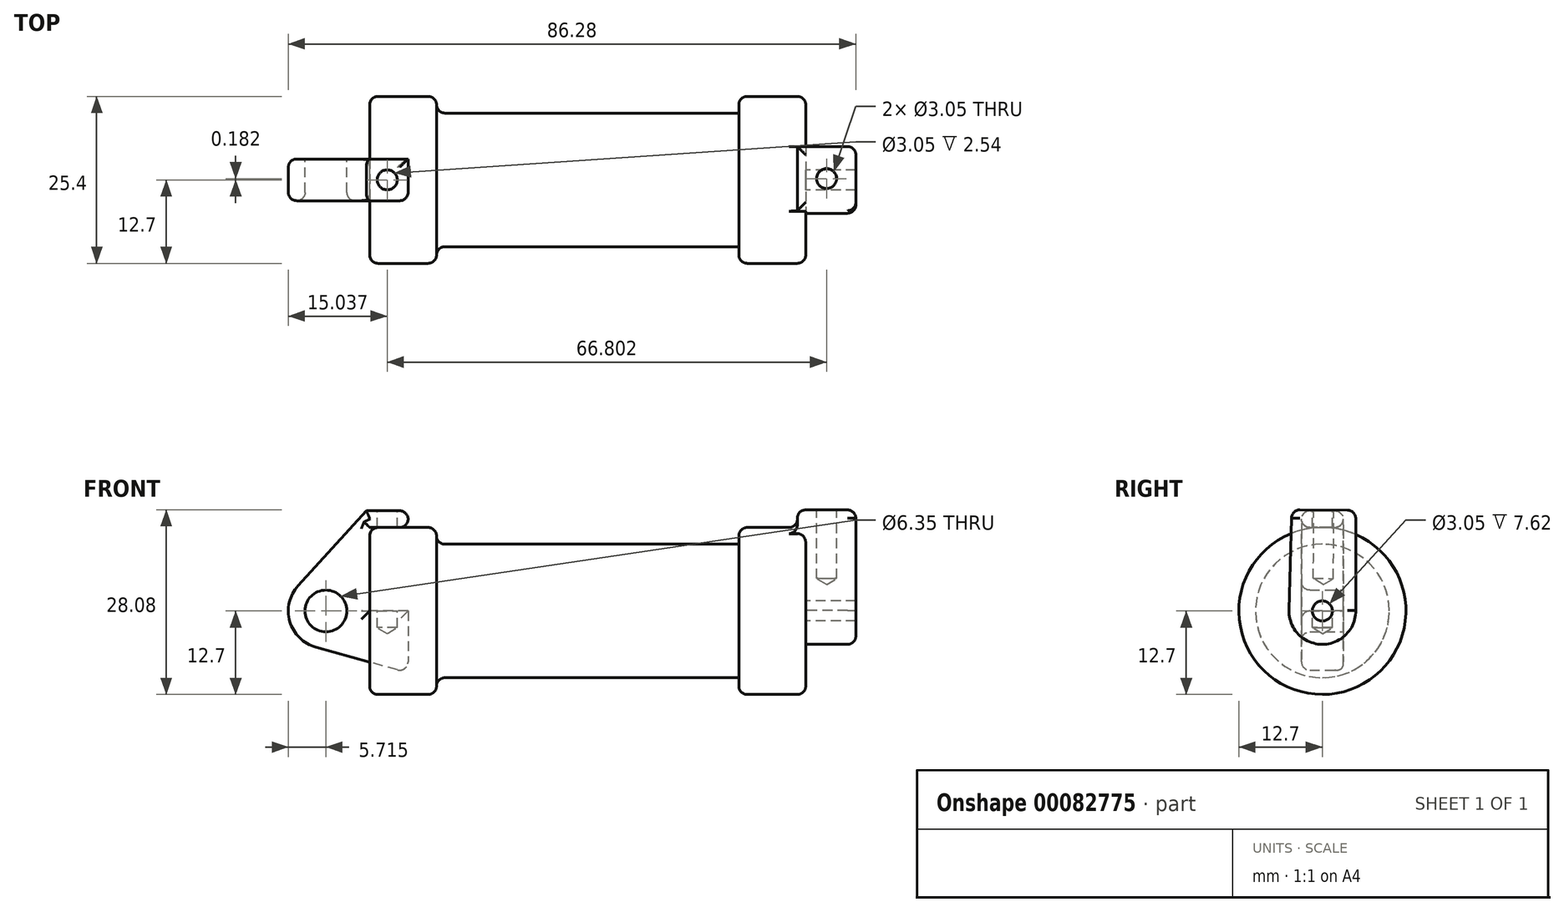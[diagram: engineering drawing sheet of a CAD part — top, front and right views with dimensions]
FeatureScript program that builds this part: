
annotation { "Feature Type Name" : "Feature", "Feature Type Description" : "" }
export const myFeature = defineFeature(function(context is Context, id is Id, definition is map)
    precondition{}
    {
        {
            var Q0;
            Q0=qCreatedBy(makeId("Front.planeOp"),FACE);
            var sketch = newSketch(context, id + "F0", { "sketchPlane" : qUnion([Q0])});
            skLineSegment(sketch, "E0", {"start": v(0, 0) * mm, "end": v(0, 12.7) * mm});
            skLineSegment(sketch, "E1", {"start": v(0, 12.7) * mm, "end": v(10.16, 12.7) * mm});
            skLineSegment(sketch, "E2", {"start": v(10.16, 12.7) * mm, "end": v(10.16, 10.16) * mm});
            skLineSegment(sketch, "E3", {"start": v(10.16, 10.16) * mm, "end": v(56.13, 10.16) * mm});
            skLineSegment(sketch, "E4", {"start": v(56.13, 10.16) * mm, "end": v(56.13, 12.7) * mm});
            skLineSegment(sketch, "E5", {"start": v(56.13, 12.7) * mm, "end": v(66.3, 12.7) * mm});
            skLineSegment(sketch, "E6", {"start": v(66.3, 12.7) * mm, "end": v(66.3, 0) * mm});
            skLineSegment(sketch, "E7", {"start": v(66.3, 0) * mm, "end": v(0, 0) * mm});
            skLineSegment(sketch, "E8", {"start": v(5.84, 15.24) * mm, "end": v(-0.5, 15.24) * mm});
            skLineSegment(sketch, "E9", {"start": v(-0.5, 15.24) * mm, "end": v(-10.88, 3.85) * mm});
            skLineSegment(sketch, "E10", {"start": v(0, 0) * mm, "end": v(-6.65, 0) * mm});
            skCircle(sketch, "E11", {"center": v(-6.65, 0) * mm, "radius": 5.72 * mm});
            skCircle(sketch, "E12", {"center": v(-6.65, 0) * mm, "radius": 3.18 * mm});
            skLineSegment(sketch, "E13", {"start": v(5.84, 15.24) * mm, "end": v(5.84, -9.4) * mm});
            skLineSegment(sketch, "E14", {"start": v(5.84, -9.4) * mm, "end": v(-8.18, -5.5) * mm});
            skSolve(sketch);
        }
        {
            var Q0;
            {var subQ0=sQuery(id+"F0.wireOp",EDGE,"E2");Q0=makeQuery(id+"F0.imprint","IMPRINT",FACE,{"disambiguationData":[TD([[makeQuery(id+"F0.imprint","IMPRINT",EDGE,{"derivedFrom":subQ0}),-1.0]])]});}
            var Q1;
            {var subQ0=sQuery(id+"F0.wireOp",EDGE,"E0");Q1=makeQuery(id+"F0.imprint","IMPRINT",FACE,{"disambiguationData":[TD([[makeQuery(id+"F0.imprint","IMPRINT",EDGE,{"derivedFrom":subQ0}),-1.0]])]});}
            var Q2;
            Q2=sQuery(id+"F0.wireOp",EDGE,"E7");
            revolve(context, id + "F1", {"entities" : qUnion([Q0, Q1]), "axis" : qUnion([Q2]), "revolveType" : RevolveType.FULL});
        }
        {
            var Q0;
            {var subQ3=sQuery(id+"F0.wireOp",EDGE,"E0");Q0=makeQuery(id+"F0.imprint","IMPRINT",FACE,{"disambiguationData":[TD([[makeQuery(id+"F0.imprint","IMPRINT",EDGE,{"derivedFrom":subQ3}),1.0]])]});}
            var Q1;
            {var subQ4=sQuery(id+"F0.wireOp",EDGE,"E12");Q1=makeQuery(id+"F0.imprint","IMPRINT",FACE,{"disambiguationData":[TD([[makeQuery(id+"F0.imprint","IMPRINT",EDGE,{"derivedFrom":subQ4}),-1.0]])]});}
            var Q2;
            {var subQ0=sQuery(id+"F0.wireOp",EDGE,"E14");Q2=makeQuery(id+"F0.imprint","IMPRINT",FACE,{"disambiguationData":[TD([[makeQuery(id+"F0.imprint","IMPRINT",EDGE,{"derivedFrom":subQ0}),-1.0]])]});}
            extrude(context, id + "F2", {"entities" : qUnion([Q0, Q1, Q2]), "endBound" : BoundingType.SYMMETRIC, "depth" : 6.35 * mm});
        }
        {
            var Q0;
            Q0=makeQuery(id+"F1.opRevolve","SWEPT_FACE",FACE,{"disambiguationData":[OSD([sQuery(id+"F0.wireOp",EDGE,"E6")])]});
            var sketch = newSketch(context, id + "F3", { "sketchPlane" : qUnion([Q0])});
            skCircle(sketch, "E15", {"center": v(0, 0) * mm, "radius": 1.52 * mm});
            skCircle(sketch, "E16", {"center": v(0, 0) * mm, "radius": 5.08 * mm});
            skLineSegment(sketch, "E17", {"start": v(5.08, 0.1) * mm, "end": v(5.08, 15.33) * mm});
            skLineSegment(sketch, "E18", {"start": v(-5.08, 0.14) * mm, "end": v(-4.66, 15.38) * mm});
            skLineSegment(sketch, "E19", {"start": v(-4.66, 15.38) * mm, "end": v(5.08, 15.33) * mm});
            skSolve(sketch);
        }
        {
            var Q0;
            Q0 = qSketchRegion(id + "F3", true);
            extrude(context, id + "F4", {"entities" : qUnion([Q0]), "operationType" : NewBodyOperationType.ADD, "depth" : 7.62 * mm, "hasSecondDirection" : true, "secondDirectionOppositeDirection" : true, "secondDirectionDepth" : 1.27 * mm});
        }
        {
            var Q0;
            Q0=makeQuery(id+"F2.opExtrude","SWEPT_FACE",FACE,{"disambiguationData":[OSD([sQuery(id+"F0.wireOp",EDGE,"E8")])]});
            var sketch = newSketch(context, id + "F5", { "sketchPlane" : qUnion([Q0])});
            skLineSegment(sketch, "E20", {"start": v(-0.5, 0) * mm, "end": v(5.84, 0) * mm, "construction": true});
            skLineSegment(sketch, "E21", {"start": v(2.67, 3.18) * mm, "end": v(2.67, -3.18) * mm, "construction": true});
            skCircle(sketch, "E22", {"center": v(2.67, 0) * mm, "radius": 1.52 * mm});
            skSolve(sketch);
        }
        {
            var Q0;
            Q0=sQuery(id+"F5.wireOp",VERTEX,"E22.center");
            var Q1;
            Q1=makeQuery(id+"F2.opExtrude","SWEPT_BODY",BODY,{"disambiguationData":[OSD([sQuery(id+"F0.wireOp",EDGE,"E0"),sQuery(id+"F0.wireOp",EDGE,"E1"),sQuery(id+"F0.wireOp",EDGE,"E7"),sQuery(id+"F0.wireOp",EDGE,"E8"),sQuery(id+"F0.wireOp",EDGE,"E9"),sQuery(id+"F0.wireOp",EDGE,"E11"),sQuery(id+"F0.wireOp",EDGE,"E12"),sQuery(id+"F0.wireOp",EDGE,"E13"),sQuery(id+"F0.wireOp",EDGE,"E14")])]});
            hole(context, id + "F6", {"style" : HoleStyle.SIMPLE, "endStyle" : HoleEndStyle.BLIND, "holeDiameter" : 3.05 * mm, "holeDepth" : 17.78 * mm, "locations" : qUnion([Q0]), "scope" : qUnion([Q1])});
        }
        {
            var Q0;
            Q0=makeQuery(id+"F4.opExtrude","SWEPT_FACE",FACE,{"disambiguationData":[OSD([sQuery(id+"F3.wireOp",EDGE,"E19")])]});
            var sketch = newSketch(context, id + "F7", { "sketchPlane" : qUnion([Q0])});
            skLineSegment(sketch, "E23", {"start": v(65.02, 0.13) * mm, "end": v(73.91, 0.13) * mm, "construction": true});
            skLineSegment(sketch, "E24", {"start": v(69.47, 5) * mm, "end": v(69.47, -4.74) * mm, "construction": true});
            skCircle(sketch, "E25", {"center": v(69.47, 0.13) * mm, "radius": 1.52 * mm});
            skSolve(sketch);
        }
        {
            var Q0;
            Q0=sQuery(id+"F7.wireOp",VERTEX,"E25.center");
            var Q1;
            Q1=makeQuery(id+"F1.opRevolve","SWEPT_BODY",BODY,{"disambiguationData":[OSD([sQuery(id+"F0.wireOp",EDGE,"E0"),sQuery(id+"F0.wireOp",EDGE,"E1"),sQuery(id+"F0.wireOp",EDGE,"E2"),sQuery(id+"F0.wireOp",EDGE,"E3"),sQuery(id+"F0.wireOp",EDGE,"E4"),sQuery(id+"F0.wireOp",EDGE,"E5"),sQuery(id+"F0.wireOp",EDGE,"E6"),sQuery(id+"F0.wireOp",EDGE,"E7")])]});
            hole(context, id + "F8", {"style" : HoleStyle.SIMPLE, "endStyle" : HoleEndStyle.BLIND, "holeDiameter" : 3.05 * mm, "holeDepth" : 10.4 * mm, "locations" : qUnion([Q0]), "scope" : qUnion([Q1])});
        }
        {
            var Q0;
            Q0=makeQuery(id+"F1.opRevolve","SWEPT_EDGE",EDGE,{"disambiguationData":[OSD([sQuery(id+"F0.wireOp",EDGE,"E4"),sQuery(id+"F0.wireOp",EDGE,"E5")])]});
            var Q1;
            Q1=makeQuery(id+"F1.opRevolve","SWEPT_EDGE",EDGE,{"disambiguationData":[OSD([sQuery(id+"F0.wireOp",EDGE,"E1"),sQuery(id+"F0.wireOp",EDGE,"E2")])]});
            fillet(context, id + "F9", {"entities" : qUnion([Q0, Q1]), "radius" : 1.27 * mm, "tangentPropagation" : true, "allowEdgeOverflow" : false});
        }
        {
            var Q0;
            {var subQ0=sQuery(id+"F0.wireOp",EDGE,"E2");Q0=makeQuery(id+"F9.opFillet","BLEND_EDGE",EDGE,{"blendedFrom":[makeQuery(id+"F1.opRevolve","SWEPT_EDGE",EDGE,{"disambiguationData":[OSD([sQuery(id+"F0.wireOp",EDGE,"E1"),subQ0])]}),makeQuery(id+"F1.opRevolve","SWEPT_FACE",FACE,{"disambiguationData":[OSD([subQ0])]})],"blendedInto":[makeQuery(id+"F1.opRevolve","SWEPT_FACE",FACE,{"disambiguationData":[OSD([subQ0])]})]});}
            var Q1;
            {var subQ0=sQuery(id+"F0.wireOp",EDGE,"E4");Q1=makeQuery(id+"F9.opFillet","BLEND_EDGE",EDGE,{"blendedFrom":[makeQuery(id+"F1.opRevolve","SWEPT_EDGE",EDGE,{"disambiguationData":[OSD([subQ0,sQuery(id+"F0.wireOp",EDGE,"E5")])]}),makeQuery(id+"F1.opRevolve","SWEPT_FACE",FACE,{"disambiguationData":[OSD([subQ0])]})],"blendedInto":[makeQuery(id+"F1.opRevolve","SWEPT_FACE",FACE,{"disambiguationData":[OSD([subQ0])]})]});}
            var Q2;
            Q2=makeQuery(id+"F1.opRevolve","SWEPT_EDGE",EDGE,{"disambiguationData":[OSD([sQuery(id+"F0.wireOp",EDGE,"E2"),sQuery(id+"F0.wireOp",EDGE,"E3")])]});
            var Q3;
            Q3=makeQuery(id+"F1.opRevolve","SWEPT_EDGE",EDGE,{"disambiguationData":[OSD([sQuery(id+"F0.wireOp",EDGE,"E0"),sQuery(id+"F0.wireOp",EDGE,"E1")])]});
            fillet(context, id + "F10", {"entities" : qUnion([Q0, Q1, Q2, Q3]), "radius" : 1.27 * mm, "tangentPropagation" : true, "allowEdgeOverflow" : false});
        }
        {
            var Q0;
            Q0=makeQuery(id+"F1.opRevolve","SWEPT_EDGE",EDGE,{"disambiguationData":[OSD([sQuery(id+"F0.wireOp",EDGE,"E5"),sQuery(id+"F0.wireOp",EDGE,"E6")])]});
            var Q1;
            Q1=makeQuery(id+"F4.opExtrude","CAP_EDGE",EDGE,{"disambiguationData":[OSD([sQuery(id+"F3.wireOp",EDGE,"E18")])],"isStart":false});
            var Q2;
            Q2=makeQuery(id+"F4.opExtrude","CAP_EDGE",EDGE,{"disambiguationData":[OSD([sQuery(id+"F3.wireOp",EDGE,"E16")])],"isStart":false});
            var Q3;
            Q3=makeQuery(id+"F4.opExtrude","CAP_EDGE",EDGE,{"disambiguationData":[OSD([sQuery(id+"F3.wireOp",EDGE,"E17")])],"isStart":false});
            fillet(context, id + "F11", {"entities" : qUnion([Q0, Q1, Q2, Q3]), "radius" : 1.27 * mm, "tangentPropagation" : true, "allowEdgeOverflow" : false});
        }
        {
            var Q0;
            Q0=makeQuery(id+"F2.opExtrude","CAP_EDGE",EDGE,{"disambiguationData":[OSD([sQuery(id+"F0.wireOp",EDGE,"E8")])],"isStart":true});
            var Q1;
            Q1=makeQuery(id+"F2.opExtrude","SWEPT_EDGE",EDGE,{"disambiguationData":[OSD([sQuery(id+"F0.wireOp",EDGE,"E8"),sQuery(id+"F0.wireOp",EDGE,"E13")])]});
            var Q2;
            Q2=makeQuery(id+"F2.opExtrude","CAP_EDGE",EDGE,{"disambiguationData":[OSD([sQuery(id+"F0.wireOp",EDGE,"E8")])],"isStart":false});
            var Q3;
            Q3=makeQuery(id+"F2.opExtrude","CAP_EDGE",EDGE,{"disambiguationData":[OSD([sQuery(id+"F0.wireOp",EDGE,"E9")])],"isStart":false});
            var Q4;
            Q4=makeQuery(id+"F2.opExtrude","CAP_EDGE",EDGE,{"disambiguationData":[OSD([sQuery(id+"F0.wireOp",EDGE,"E11")])],"isStart":false});
            var Q5;
            Q5=makeQuery(id+"F2.opExtrude","CAP_EDGE",EDGE,{"disambiguationData":[OSD([sQuery(id+"F0.wireOp",EDGE,"E9")])],"isStart":true});
            var Q6;
            Q6=makeQuery(id+"F2.opExtrude","CAP_EDGE",EDGE,{"disambiguationData":[OSD([sQuery(id+"F0.wireOp",EDGE,"E11")])],"isStart":true});
            var Q7;
            Q7=makeQuery(id+"F4.opExtrude","CAP_EDGE",EDGE,{"disambiguationData":[OSD([sQuery(id+"F3.wireOp",EDGE,"E19")])],"isStart":true});
            var Q8;
            Q8=makeQuery(id+"F4.opExtrude","SWEPT_EDGE",EDGE,{"disambiguationData":[OSD([sQuery(id+"F3.wireOp",EDGE,"E17"),sQuery(id+"F3.wireOp",EDGE,"E19")])]});
            var Q9;
            Q9=makeQuery(id+"F11.opFillet","BLEND_EDGE",EDGE,{"blendedFrom":[makeQuery(id+"F4.opExtrude","CAP_EDGE",EDGE,{"disambiguationData":[OSD([sQuery(id+"F3.wireOp",EDGE,"E17")])],"isStart":false}),makeQuery(id+"F4.opExtrude","SWEPT_FACE",FACE,{"disambiguationData":[OSD([sQuery(id+"F3.wireOp",EDGE,"E19")])]})],"blendedInto":[makeQuery(id+"F4.opExtrude","SWEPT_FACE",FACE,{"disambiguationData":[OSD([sQuery(id+"F3.wireOp",EDGE,"E19")])]})]});
            var Q10;
            Q10=makeQuery(id+"F4.opExtrude","CAP_EDGE",EDGE,{"disambiguationData":[OSD([sQuery(id+"F3.wireOp",EDGE,"E19")])],"isStart":false});
            var Q11;
            Q11=makeQuery(id+"F11.opFillet","BLEND_EDGE",EDGE,{"blendedFrom":[makeQuery(id+"F4.opExtrude","CAP_EDGE",EDGE,{"disambiguationData":[OSD([sQuery(id+"F3.wireOp",EDGE,"E18")])],"isStart":false}),makeQuery(id+"F4.opExtrude","SWEPT_FACE",FACE,{"disambiguationData":[OSD([sQuery(id+"F3.wireOp",EDGE,"E19")])]})],"blendedInto":[makeQuery(id+"F4.opExtrude","SWEPT_FACE",FACE,{"disambiguationData":[OSD([sQuery(id+"F3.wireOp",EDGE,"E19")])]})]});
            var Q12;
            Q12=makeQuery(id+"F4.opExtrude","SWEPT_EDGE",EDGE,{"disambiguationData":[OSD([sQuery(id+"F3.wireOp",EDGE,"E18"),sQuery(id+"F3.wireOp",EDGE,"E19")])]});
            var Q13;
            Q13=makeQuery(id+"F2.opExtrude","SWEPT_EDGE",EDGE,{"disambiguationData":[OSD([sQuery(id+"F0.wireOp",EDGE,"E1"),sQuery(id+"F0.wireOp",EDGE,"E13")])]});
            var Q14;
            {var subQ0=sQuery(id+"F0.wireOp",EDGE,"E5");Q14=makeQuery(id+"F11.opFillet","BLEND_EDGE",EDGE,{"blendedFrom":[makeQuery(id+"F1.opRevolve","SWEPT_EDGE",EDGE,{"disambiguationData":[OSD([subQ0,sQuery(id+"F0.wireOp",EDGE,"E6")])]}),makeQuery(id+"F1.opRevolve","SWEPT_FACE",FACE,{"disambiguationData":[OSD([subQ0])]})],"blendedInto":[makeQuery(id+"F1.opRevolve","SWEPT_FACE",FACE,{"disambiguationData":[OSD([subQ0])]})]});}
            var Q15;
            Q15=makeQuery(id+"F4.boolean.opBoolean","INTERSECT",EDGE,{"derivedFrom":[makeQuery(id+"F1.opRevolve","SWEPT_FACE",FACE,{"disambiguationData":[OSD([sQuery(id+"F0.wireOp",EDGE,"E5")])]}),makeQuery(id+"F4.opExtrude","CAP_FACE",FACE,{"disambiguationData":[OSD([sQuery(id+"F3.wireOp",EDGE,"E15"),sQuery(id+"F3.wireOp",EDGE,"E16"),sQuery(id+"F3.wireOp",EDGE,"E17"),sQuery(id+"F3.wireOp",EDGE,"E18"),sQuery(id+"F3.wireOp",EDGE,"E19")])],"isStart":true})]});
            var Q16;
            Q16=makeQuery(id+"F1.opRevolve","SWEPT_FACE",FACE,{"disambiguationData":[OSD([sQuery(id+"F0.wireOp",EDGE,"E1")])]});
            var Q17;
            Q17=makeQuery(id+"F2.opExtrude","CAP_EDGE",EDGE,{"disambiguationData":[OSD([sQuery(id+"F0.wireOp",EDGE,"E1")])],"isStart":true});
            var Q18;
            Q18=makeQuery(id+"F2.opExtrude","CAP_EDGE",EDGE,{"disambiguationData":[OSD([sQuery(id+"F0.wireOp",EDGE,"E0")])],"isStart":true});
            var Q19;
            Q19=makeQuery(id+"F1.opRevolve","SWEPT_FACE",FACE,{"disambiguationData":[OSD([sQuery(id+"F0.wireOp",EDGE,"E0")])]});
            var Q20;
            Q20=makeQuery(id+"F2.opExtrude","SWEPT_FACE",FACE,{"disambiguationData":[OSD([sQuery(id+"F0.wireOp",EDGE,"E14")])]});
            var Q21;
            Q21=makeQuery(id+"F2.opExtrude","CAP_FACE",FACE,{"disambiguationData":[OSD([sQuery(id+"F0.wireOp",EDGE,"E0"),sQuery(id+"F0.wireOp",EDGE,"E1"),sQuery(id+"F0.wireOp",EDGE,"E7"),sQuery(id+"F0.wireOp",EDGE,"E8"),sQuery(id+"F0.wireOp",EDGE,"E9"),sQuery(id+"F0.wireOp",EDGE,"E11"),sQuery(id+"F0.wireOp",EDGE,"E12"),sQuery(id+"F0.wireOp",EDGE,"E13"),sQuery(id+"F0.wireOp",EDGE,"E14")])],"isStart":false});
            fillet(context, id + "F12", {"entities" : qUnion([Q0, Q1, Q2, Q3, Q4, Q5, Q6, Q7, Q8, Q9, Q10, Q11, Q12, Q13, Q14, Q15, Q16, Q17, Q18, Q19, Q20, Q21]), "radius" : 1.27 * mm, "tangentPropagation" : true, "allowEdgeOverflow" : false});
        }
    });
